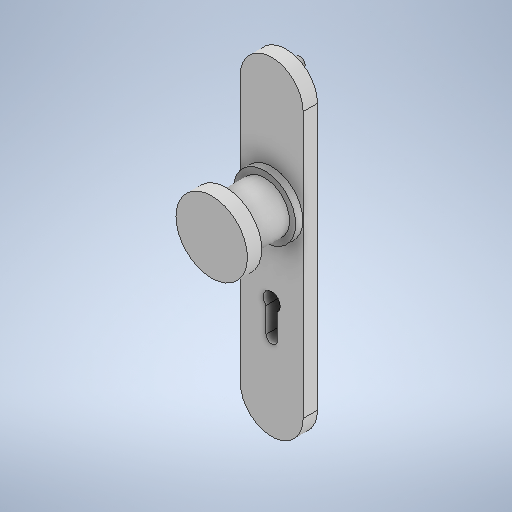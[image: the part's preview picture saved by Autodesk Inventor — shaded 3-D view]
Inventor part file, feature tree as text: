
AUTODESK INVENTOR PART (.ipt)
format: ipt  version: 2025.1 (Build 291241000, 241)  size: 311,808 bytes
history: native  units: mm
features: sketch x4, extrude x3, revolve x1, fillet x1
ambient origin geometry x8: Origin, YZ Plane, XZ Plane, XY Plane, X Axis, Y Axis, Z Axis, Center Point
bodies: Solid1 (feature_tree)
feature tree (9):
  revolve  "Revolution1"  [1 undecoded]
  extrude  "Extrusion2"  TaperAngle=90.0deg  [1 undecoded]
  fillet  "Fillet2"  Radius=37.0mm
  extrude  "Extrusion3"  Depth=5.0mm
  extrude  "Extrusion4"  Depth=10.0mm
  sketch  "Sketch1"  dims[d1=50.0mm d3=10.0mm]
  sketch  "Sketch3"  dims[d4=35.0mm d5=90.0deg d12=37.0mm]
  sketch  "Sketch4"  dims[d13=5.0mm d14=43.5mm]
  sketch  "Sketch5"  dims[d16=44.0mm d17=88.0mm d18=230.0mm d19=10.0mm d20=0.0mm d22=2.0mm d23=7.0mm d24=21.5mm d25=90.5mm d26=75.0mm d27=10.0mm d28=0.0mm d29=60.0mm d30=12.0mm d31=4.0mm d32=22.0mm d33=10.0mm d34=0.0mm]
note: 2 required parameter values undecoded (feature->parameter linkage not recoverable at this tier; creation-order binding heuristic only, values carry confidence <= 0.55)